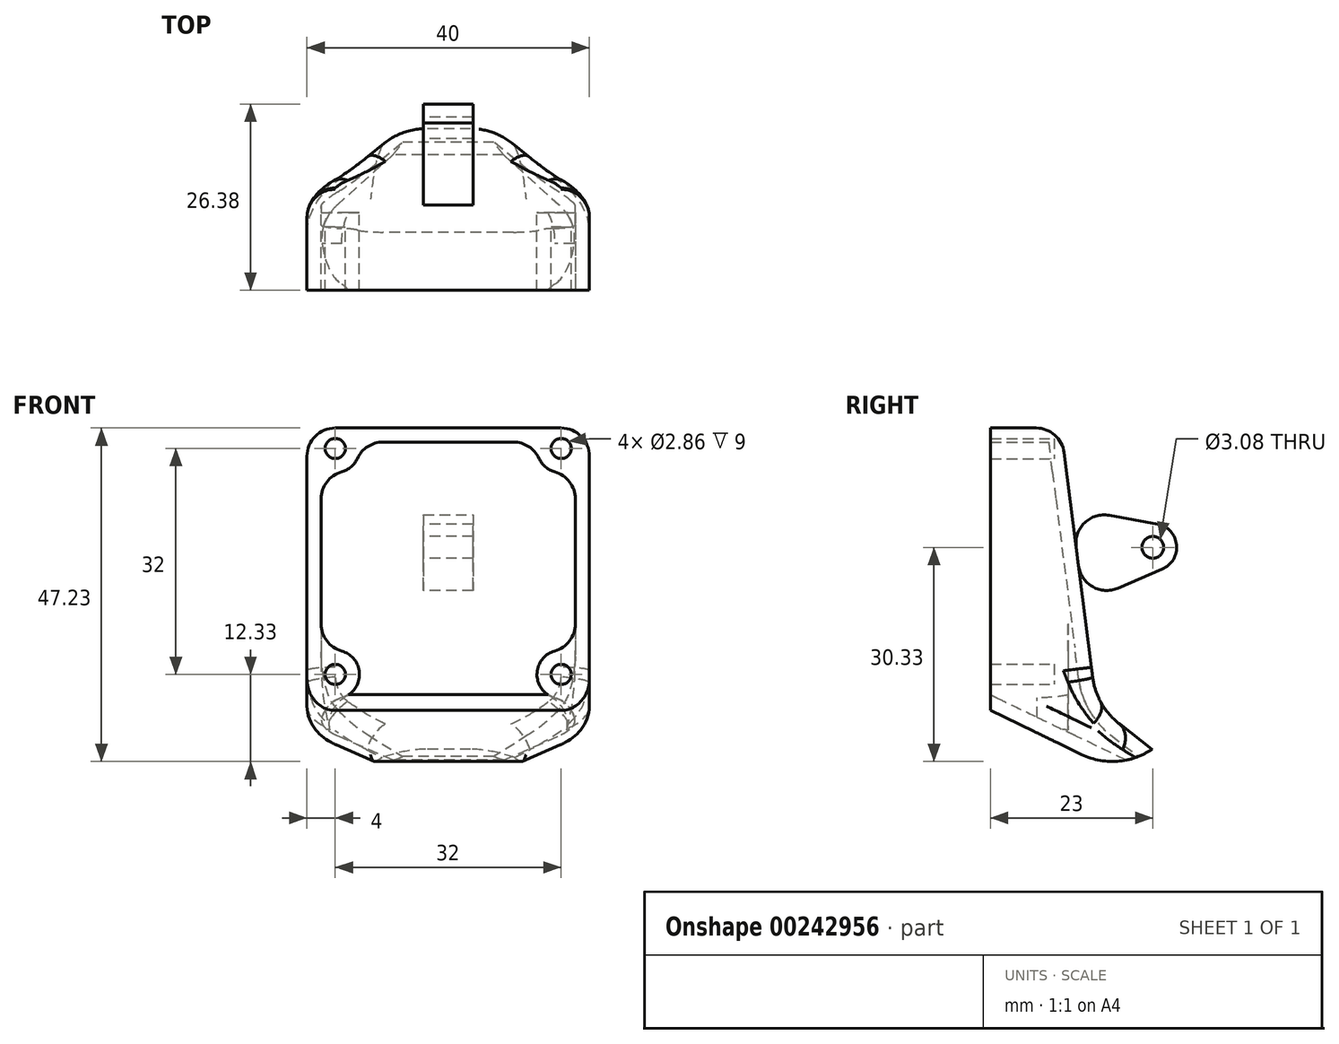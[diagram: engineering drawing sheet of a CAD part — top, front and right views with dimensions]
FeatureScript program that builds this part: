
annotation { "Feature Type Name" : "Feature", "Feature Type Description" : "" }
export const myFeature = defineFeature(function(context is Context, id is Id, definition is map)
    precondition{}
    {
        {
            var Q0;
            Q0=qCreatedBy(makeId("Front.planeOp"),FACE);
            var sketch = newSketch(context, id + "F0", { "sketchPlane" : qUnion([Q0])});
            skLineSegment(sketch, "E0.bottom", {"start": v(-20, 20) * mm, "end": v(20, 20) * mm});
            skLineSegment(sketch, "E0.top", {"start": v(-20, -20) * mm, "end": v(20, -20) * mm});
            skLineSegment(sketch, "E0.left", {"start": v(-20, 20) * mm, "end": v(-20, -20) * mm});
            skLineSegment(sketch, "E0.right", {"start": v(20, 20) * mm, "end": v(20, -20) * mm});
            skLineSegment(sketch, "E1", {"start": v(-8, -32) * mm, "end": v(8, -32) * mm});
            skLineSegment(sketch, "E2", {"start": v(-20, -20) * mm, "end": v(-8, -32) * mm});
            skLineSegment(sketch, "E3.MirrorCS", {"start": v(20, -20) * mm, "end": v(8, -32) * mm});
            skPoint(sketch, "E4.start.orphan", {"position": v(20, -32) * mm});
            skCircle(sketch, "E5", {"center": v(-16, 16) * mm, "radius": 1.43 * mm});
            skCircle(sketch, "E6", {"center": v(16, 16) * mm, "radius": 1.43 * mm});
            skCircle(sketch, "E7", {"center": v(16, -16) * mm, "radius": 1.43 * mm});
            skCircle(sketch, "E8", {"center": v(-16, -16) * mm, "radius": 1.43 * mm});
            skSolve(sketch);
        }
        {
            var Q0;
            Q0=qCreatedBy(makeId("Right.planeOp"),FACE);
            var sketch = newSketch(context, id + "F1", { "sketchPlane" : qUnion([Q0])});
            skLineSegment(sketch, "E9", {"start": v(-5, 18.9) * mm, "end": v(-5, -21.1) * mm});
            skLineSegment(sketch, "E10", {"start": v(-5, -21.1) * mm, "end": v(15.71, -31.1) * mm});
            skLineSegment(sketch, "E11", {"start": v(15.71, -31.1) * mm, "end": v(17.89, -26.6) * mm});
            skLineSegment(sketch, "E12", {"start": v(5, 18.9) * mm, "end": v(-5, 18.9) * mm});
            skLineSegment(sketch, "E13", {"start": v(5, 18.9) * mm, "end": v(10, -20.48) * mm});
            skLineSegment(sketch, "E14", {"start": v(10, -20.48) * mm, "end": v(17.89, -26.6) * mm});
            skCircle(sketch, "E15", {"center": v(18, 2) * mm, "radius": 1.54 * mm});
            skArc(sketch, "E16", {"start": v(19.32, -1.1) * mm, "mid": v(21.36, 2.33) * mm, "end": v(18.7, 5.3) * mm});
            skLineSegment(sketch, "E17", {"start": v(6.45, 7.48) * mm, "end": v(8.15, -5.87) * mm});
            skLineSegment(sketch, "E18", {"start": v(6.45, 7.48) * mm, "end": v(18.7, 5.3) * mm});
            skLineSegment(sketch, "E19", {"start": v(8.15, -5.87) * mm, "end": v(19.32, -1.1) * mm});
            skSolve(sketch);
        }
        {
            var Q0;
            Q0=makeQuery(id+"F1.imprint","IMPRINT",FACE,{"disambiguationData":[TD([[makeQuery(id+"F1.imprint","IMPRINT",EDGE,{"derivedFrom":sQuery(id+"F1.wireOp",EDGE,"E9")}),1.0]])]});
            extrude(context, id + "F2", {"entities" : qUnion([Q0]), "endBound" : BoundingType.SYMMETRIC, "depth" : 40 * mm});
        }
        {
            var Q0;
            Q0=makeQuery(id+"F2.opExtrude","CAP_EDGE",EDGE,{"disambiguationData":[OSD([sQuery(id+"F1.wireOp",EDGE,"E11")])],"isStart":false});
            var Q1;
            Q1=makeQuery(id+"F2.opExtrude","CAP_EDGE",EDGE,{"disambiguationData":[OSD([sQuery(id+"F1.wireOp",EDGE,"E11")])],"isStart":true});
            chamfer(context, id + "F3", {"entities" : qUnion([Q0, Q1]), "width" : 12 * mm, "tangentPropagation" : true});
        }
        {
            var Q0;
            {var subQ0=sQuery(id+"F1.wireOp",EDGE,"E11");Q0=makeQuery(id+"F3.opChamfer","BLEND_EDGE",EDGE,{"blendedFrom":[makeQuery(id+"F2.opExtrude","CAP_EDGE",EDGE,{"disambiguationData":[OSD([subQ0])],"isStart":true}),makeQuery(id+"F2.opExtrude","CAP_FACE",FACE,{"disambiguationData":[OSD([sQuery(id+"F1.wireOp",EDGE,"E9"),sQuery(id+"F1.wireOp",EDGE,"E10"),subQ0,sQuery(id+"F1.wireOp",EDGE,"E12"),sQuery(id+"F1.wireOp",EDGE,"E13"),sQuery(id+"F1.wireOp",EDGE,"E14"),sQuery(id+"F1.wireOp",EDGE,"E17")])],"isStart":true})],"blendedInto":[makeQuery(id+"F2.opExtrude","CAP_FACE",FACE,{"disambiguationData":[OSD([sQuery(id+"F1.wireOp",EDGE,"E9"),sQuery(id+"F1.wireOp",EDGE,"E10"),subQ0,sQuery(id+"F1.wireOp",EDGE,"E12"),sQuery(id+"F1.wireOp",EDGE,"E13"),sQuery(id+"F1.wireOp",EDGE,"E14"),sQuery(id+"F1.wireOp",EDGE,"E17")])],"isStart":true})]});}
            var Q1;
            {var subQ0=sQuery(id+"F1.wireOp",EDGE,"E11");Q1=makeQuery(id+"F3.opChamfer","BLEND_EDGE",EDGE,{"blendedFrom":[makeQuery(id+"F2.opExtrude","CAP_EDGE",EDGE,{"disambiguationData":[OSD([subQ0])],"isStart":false}),makeQuery(id+"F2.opExtrude","CAP_FACE",FACE,{"disambiguationData":[OSD([sQuery(id+"F1.wireOp",EDGE,"E9"),sQuery(id+"F1.wireOp",EDGE,"E10"),subQ0,sQuery(id+"F1.wireOp",EDGE,"E12"),sQuery(id+"F1.wireOp",EDGE,"E13"),sQuery(id+"F1.wireOp",EDGE,"E14"),sQuery(id+"F1.wireOp",EDGE,"E17")])],"isStart":false})],"blendedInto":[makeQuery(id+"F2.opExtrude","CAP_FACE",FACE,{"disambiguationData":[OSD([sQuery(id+"F1.wireOp",EDGE,"E9"),sQuery(id+"F1.wireOp",EDGE,"E10"),subQ0,sQuery(id+"F1.wireOp",EDGE,"E12"),sQuery(id+"F1.wireOp",EDGE,"E13"),sQuery(id+"F1.wireOp",EDGE,"E14"),sQuery(id+"F1.wireOp",EDGE,"E17")])],"isStart":false})]});}
            var Q2;
            Q2=makeQuery(id+"F2.opExtrude","SWEPT_EDGE",EDGE,{"disambiguationData":[OSD([sQuery(id+"F1.wireOp",EDGE,"E13"),sQuery(id+"F1.wireOp",EDGE,"E14")])]});
            fillet(context, id + "F4", {"entities" : qUnion([Q0, Q1, Q2]), "radius" : 10 * mm, "tangentPropagation" : true, "allowEdgeOverflow" : false});
        }
        {
            var Q0;
            Q0=qCreatedBy(makeId("Front.planeOp"),FACE);
            var sketch = newSketch(context, id + "F5", { "sketchPlane" : qUnion([Q0])});
            skCircle(sketch, "E20", {"center": v(-16, 16) * mm, "radius": 1.43 * mm});
            skCircle(sketch, "E21", {"center": v(16, 16) * mm, "radius": 1.43 * mm});
            skCircle(sketch, "E22", {"center": v(16, -16) * mm, "radius": 1.43 * mm});
            skCircle(sketch, "E23", {"center": v(-16, -16) * mm, "radius": 1.43 * mm});
            skSolve(sketch);
        }
        {
            var Q0;
            Q0=makeQuery(id+"F5.imprint","IMPRINT",FACE,{"disambiguationData":[TD([[makeQuery(id+"F5.imprint","IMPRINT",EDGE,{"derivedFrom":sQuery(id+"F5.wireOp",EDGE,"E20")}),1.0]])]});
            var Q1;
            Q1=makeQuery(id+"F5.imprint","IMPRINT",FACE,{"disambiguationData":[TD([[makeQuery(id+"F5.imprint","IMPRINT",EDGE,{"derivedFrom":sQuery(id+"F5.wireOp",EDGE,"E21")}),1.0]])]});
            var Q2;
            Q2=makeQuery(id+"F5.imprint","IMPRINT",FACE,{"disambiguationData":[TD([[makeQuery(id+"F5.imprint","IMPRINT",EDGE,{"derivedFrom":sQuery(id+"F5.wireOp",EDGE,"E23")}),1.0]])]});
            var Q3;
            Q3=makeQuery(id+"F5.imprint","IMPRINT",FACE,{"disambiguationData":[TD([[makeQuery(id+"F5.imprint","IMPRINT",EDGE,{"derivedFrom":sQuery(id+"F5.wireOp",EDGE,"E22")}),1.0]])]});
            var Q4;
            Q4=sQuery(id+"F5.wireOp",EDGE,"E21");
            var Q5;
            Q5=sQuery(id+"F5.wireOp",EDGE,"E20");
            var Q6;
            Q6=sQuery(id+"F5.wireOp",EDGE,"E22");
            var Q7;
            Q7=sQuery(id+"F5.wireOp",EDGE,"E23");
            var Q8;
            Q8=makeQuery(id+"F2.opExtrude","SWEPT_FACE",FACE,{"disambiguationData":[OSD([sQuery(id+"F1.wireOp",EDGE,"E9")])]});
            extrude(context, id + "F6", {"entities" : qUnion([Q0, Q1, Q2, Q3]), "operationType" : NewBodyOperationType.REMOVE, "surfaceEntities" : qUnion([Q4, Q5, Q6, Q7]), "endBound" : BoundingType.UP_TO_SURFACE, "endBoundEntityFace" : qUnion([Q8]), "depth" : 20 * mm, "hasSecondDirection" : true, "secondDirectionOppositeDirection" : true, "secondDirectionDepth" : 4 * mm});
        }
        {
            var Q0;
            Q0=makeQuery(id+"F2.opExtrude","SWEPT_FACE",FACE,{"disambiguationData":[OSD([sQuery(id+"F1.wireOp",EDGE,"E9")])]});
            var Q1;
            Q1=makeQuery(id+"F2.opExtrude","SWEPT_FACE",FACE,{"disambiguationData":[OSD([sQuery(id+"F1.wireOp",EDGE,"E11")])]});
            shell(context, id + "F7", {"entities" : qUnion([Q0, Q1]), "thickness" : 2 * mm});
        }
        {
            var Q0;
            Q0=makeQuery(id+"F2.opExtrude","CAP_EDGE",EDGE,{"disambiguationData":[OSD([sQuery(id+"F1.wireOp",EDGE,"E12")])],"isStart":false});
            var Q1;
            Q1=makeQuery(id+"F2.opExtrude","CAP_EDGE",EDGE,{"disambiguationData":[OSD([sQuery(id+"F1.wireOp",EDGE,"E12")])],"isStart":true});
            var Q2;
            Q2=makeQuery(id+"F2.opExtrude","CAP_EDGE",EDGE,{"disambiguationData":[OSD([sQuery(id+"F1.wireOp",EDGE,"E10")])],"isStart":false});
            var Q3;
            Q3=makeQuery(id+"F2.opExtrude","CAP_EDGE",EDGE,{"disambiguationData":[OSD([sQuery(id+"F1.wireOp",EDGE,"E10")])],"isStart":true});
            var Q4;
            Q4=makeQuery(id+"F2.opExtrude","CAP_EDGE",EDGE,{"disambiguationData":[OSD([sQuery(id+"F1.wireOp",EDGE,"E13"),sQuery(id+"F1.wireOp",EDGE,"E17")])],"isStart":true});
            var Q5;
            Q5=makeQuery(id+"F2.opExtrude","CAP_EDGE",EDGE,{"disambiguationData":[OSD([sQuery(id+"F1.wireOp",EDGE,"E13"),sQuery(id+"F1.wireOp",EDGE,"E17")])],"isStart":false});
            var Q6;
            Q6=makeQuery(id+"F2.opExtrude","SWEPT_EDGE",EDGE,{"disambiguationData":[OSD([sQuery(id+"F1.wireOp",EDGE,"E12"),sQuery(id+"F1.wireOp",EDGE,"E13")])]});
            fillet(context, id + "F8", {"entities" : qUnion([Q0, Q1, Q2, Q3, Q4, Q5, Q6]), "radius" : 4 * mm, "tangentPropagation" : true, "allowEdgeOverflow" : false});
        }
        {
            var Q0;
            Q0=makeQuery(id+"F1.imprint","IMPRINT",FACE,{"disambiguationData":[TD([[makeQuery(id+"F1.imprint","IMPRINT",EDGE,{"derivedFrom":sQuery(id+"F1.wireOp",EDGE,"E15")}),-1.0]])]});
            extrude(context, id + "F9", {"entities" : qUnion([Q0]), "operationType" : NewBodyOperationType.ADD, "endBound" : BoundingType.SYMMETRIC, "depth" : 7 * mm});
        }
        {
            var Q0;
            Q0=makeQuery(id+"F9.opExtrude","SWEPT_EDGE",EDGE,{"disambiguationData":[OSD([sQuery(id+"F1.wireOp",EDGE,"E13"),sQuery(id+"F1.wireOp",EDGE,"E17"),sQuery(id+"F1.wireOp",EDGE,"E18")])]});
            var Q1;
            Q1=makeQuery(id+"F9.opExtrude","SWEPT_EDGE",EDGE,{"disambiguationData":[OSD([sQuery(id+"F1.wireOp",EDGE,"E13"),sQuery(id+"F1.wireOp",EDGE,"E17"),sQuery(id+"F1.wireOp",EDGE,"E19")])]});
            fillet(context, id + "F10", {"entities" : qUnion([Q0, Q1]), "radius" : 4 * mm, "tangentPropagation" : true, "allowEdgeOverflow" : false});
        }
        {
            var Q0;
            Q0=makeQuery(id+"F2.opExtrude","SWEPT_EDGE",EDGE,{"disambiguationData":[OSD([sQuery(id+"F1.wireOp",EDGE,"E10"),sQuery(id+"F1.wireOp",EDGE,"E11")])]});
            fillet(context, id + "F11", {"entities" : qUnion([Q0]), "radius" : 10 * mm, "tangentPropagation" : true, "allowEdgeOverflow" : false});
        }
        {
            var Q0;
            Q0=makeQuery(id+"F7.opShell","TWEAK_EDGE",EDGE,{"derivedFrom":[makeQuery(id+"F2.opExtrude","SWEPT_FACE",FACE,{"disambiguationData":[OSD([sQuery(id+"F1.wireOp",EDGE,"E12")])]}),makeQuery(id+"F6.boolean.opBoolean","COPY",FACE,{"derivedFrom":makeQuery(id+"F6.opExtrude","SWEPT_FACE",FACE,{"disambiguationData":[OSD([sQuery(id+"F5.wireOp",EDGE,"E20")])]})})]});
            var Q1;
            Q1=makeQuery(id+"F7.opShell","TWEAK_EDGE",EDGE,{"derivedFrom":[makeQuery(id+"F2.opExtrude","CAP_FACE",FACE,{"disambiguationData":[OSD([sQuery(id+"F1.wireOp",EDGE,"E9"),sQuery(id+"F1.wireOp",EDGE,"E10"),sQuery(id+"F1.wireOp",EDGE,"E11"),sQuery(id+"F1.wireOp",EDGE,"E12"),sQuery(id+"F1.wireOp",EDGE,"E13"),sQuery(id+"F1.wireOp",EDGE,"E14"),sQuery(id+"F1.wireOp",EDGE,"E17")])],"isStart":true}),makeQuery(id+"F6.boolean.opBoolean","COPY",FACE,{"derivedFrom":makeQuery(id+"F6.opExtrude","SWEPT_FACE",FACE,{"disambiguationData":[OSD([sQuery(id+"F5.wireOp",EDGE,"E20")])]})})]});
            var Q2;
            Q2=makeQuery(id+"F7.opShell","TWEAK_EDGE",EDGE,{"derivedFrom":[makeQuery(id+"F2.opExtrude","SWEPT_FACE",FACE,{"disambiguationData":[OSD([sQuery(id+"F1.wireOp",EDGE,"E12")])]}),makeQuery(id+"F6.boolean.opBoolean","COPY",FACE,{"derivedFrom":makeQuery(id+"F6.opExtrude","SWEPT_FACE",FACE,{"disambiguationData":[OSD([sQuery(id+"F5.wireOp",EDGE,"E21")])]})})]});
            var Q3;
            Q3=makeQuery(id+"F7.opShell","TWEAK_EDGE",EDGE,{"derivedFrom":[makeQuery(id+"F2.opExtrude","CAP_FACE",FACE,{"disambiguationData":[OSD([sQuery(id+"F1.wireOp",EDGE,"E9"),sQuery(id+"F1.wireOp",EDGE,"E10"),sQuery(id+"F1.wireOp",EDGE,"E11"),sQuery(id+"F1.wireOp",EDGE,"E12"),sQuery(id+"F1.wireOp",EDGE,"E13"),sQuery(id+"F1.wireOp",EDGE,"E14"),sQuery(id+"F1.wireOp",EDGE,"E17")])],"isStart":false}),makeQuery(id+"F6.boolean.opBoolean","COPY",FACE,{"derivedFrom":makeQuery(id+"F6.opExtrude","SWEPT_FACE",FACE,{"disambiguationData":[OSD([sQuery(id+"F5.wireOp",EDGE,"E21")])]})})]});
            var Q4;
            Q4=makeQuery(id+"F7.opShell","TWEAK_EDGE",EDGE,{"disambiguationData":[OD(1.0)],"derivedFrom":[makeQuery(id+"F2.opExtrude","CAP_FACE",FACE,{"disambiguationData":[OSD([sQuery(id+"F1.wireOp",EDGE,"E9"),sQuery(id+"F1.wireOp",EDGE,"E10"),sQuery(id+"F1.wireOp",EDGE,"E11"),sQuery(id+"F1.wireOp",EDGE,"E12"),sQuery(id+"F1.wireOp",EDGE,"E13"),sQuery(id+"F1.wireOp",EDGE,"E14"),sQuery(id+"F1.wireOp",EDGE,"E17")])],"isStart":true}),makeQuery(id+"F6.boolean.opBoolean","COPY",FACE,{"derivedFrom":makeQuery(id+"F6.opExtrude","SWEPT_FACE",FACE,{"disambiguationData":[OSD([sQuery(id+"F5.wireOp",EDGE,"E23")])]})})]});
            var Q5;
            Q5=makeQuery(id+"F7.opShell","TWEAK_EDGE",EDGE,{"disambiguationData":[OD(1.0)],"derivedFrom":[makeQuery(id+"F2.opExtrude","CAP_FACE",FACE,{"disambiguationData":[OSD([sQuery(id+"F1.wireOp",EDGE,"E9"),sQuery(id+"F1.wireOp",EDGE,"E10"),sQuery(id+"F1.wireOp",EDGE,"E11"),sQuery(id+"F1.wireOp",EDGE,"E12"),sQuery(id+"F1.wireOp",EDGE,"E13"),sQuery(id+"F1.wireOp",EDGE,"E14"),sQuery(id+"F1.wireOp",EDGE,"E17")])],"isStart":false}),makeQuery(id+"F6.boolean.opBoolean","COPY",FACE,{"derivedFrom":makeQuery(id+"F6.opExtrude","SWEPT_FACE",FACE,{"disambiguationData":[OSD([sQuery(id+"F5.wireOp",EDGE,"E22")])]})})]});
            var Q6;
            Q6=makeQuery(id+"F7.opShell","TWEAK_EDGE",EDGE,{"disambiguationData":[OD(0.0)],"derivedFrom":[makeQuery(id+"F2.opExtrude","CAP_FACE",FACE,{"disambiguationData":[OSD([sQuery(id+"F1.wireOp",EDGE,"E9"),sQuery(id+"F1.wireOp",EDGE,"E10"),sQuery(id+"F1.wireOp",EDGE,"E11"),sQuery(id+"F1.wireOp",EDGE,"E12"),sQuery(id+"F1.wireOp",EDGE,"E13"),sQuery(id+"F1.wireOp",EDGE,"E14"),sQuery(id+"F1.wireOp",EDGE,"E17")])],"isStart":true}),makeQuery(id+"F6.boolean.opBoolean","COPY",FACE,{"derivedFrom":makeQuery(id+"F6.opExtrude","SWEPT_FACE",FACE,{"disambiguationData":[OSD([sQuery(id+"F5.wireOp",EDGE,"E23")])]})})]});
            var Q7;
            Q7=makeQuery(id+"F7.opShell","TWEAK_EDGE",EDGE,{"disambiguationData":[OD(0.0)],"derivedFrom":[makeQuery(id+"F2.opExtrude","CAP_FACE",FACE,{"disambiguationData":[OSD([sQuery(id+"F1.wireOp",EDGE,"E9"),sQuery(id+"F1.wireOp",EDGE,"E10"),sQuery(id+"F1.wireOp",EDGE,"E11"),sQuery(id+"F1.wireOp",EDGE,"E12"),sQuery(id+"F1.wireOp",EDGE,"E13"),sQuery(id+"F1.wireOp",EDGE,"E14"),sQuery(id+"F1.wireOp",EDGE,"E17")])],"isStart":false}),makeQuery(id+"F6.boolean.opBoolean","COPY",FACE,{"derivedFrom":makeQuery(id+"F6.opExtrude","SWEPT_FACE",FACE,{"disambiguationData":[OSD([sQuery(id+"F5.wireOp",EDGE,"E22")])]})})]});
            fillet(context, id + "F12", {"entities" : qUnion([Q0, Q1, Q2, Q3, Q4, Q5, Q6, Q7]), "radius" : 4 * mm, "tangentPropagation" : true, "allowEdgeOverflow" : false});
        }
    });
